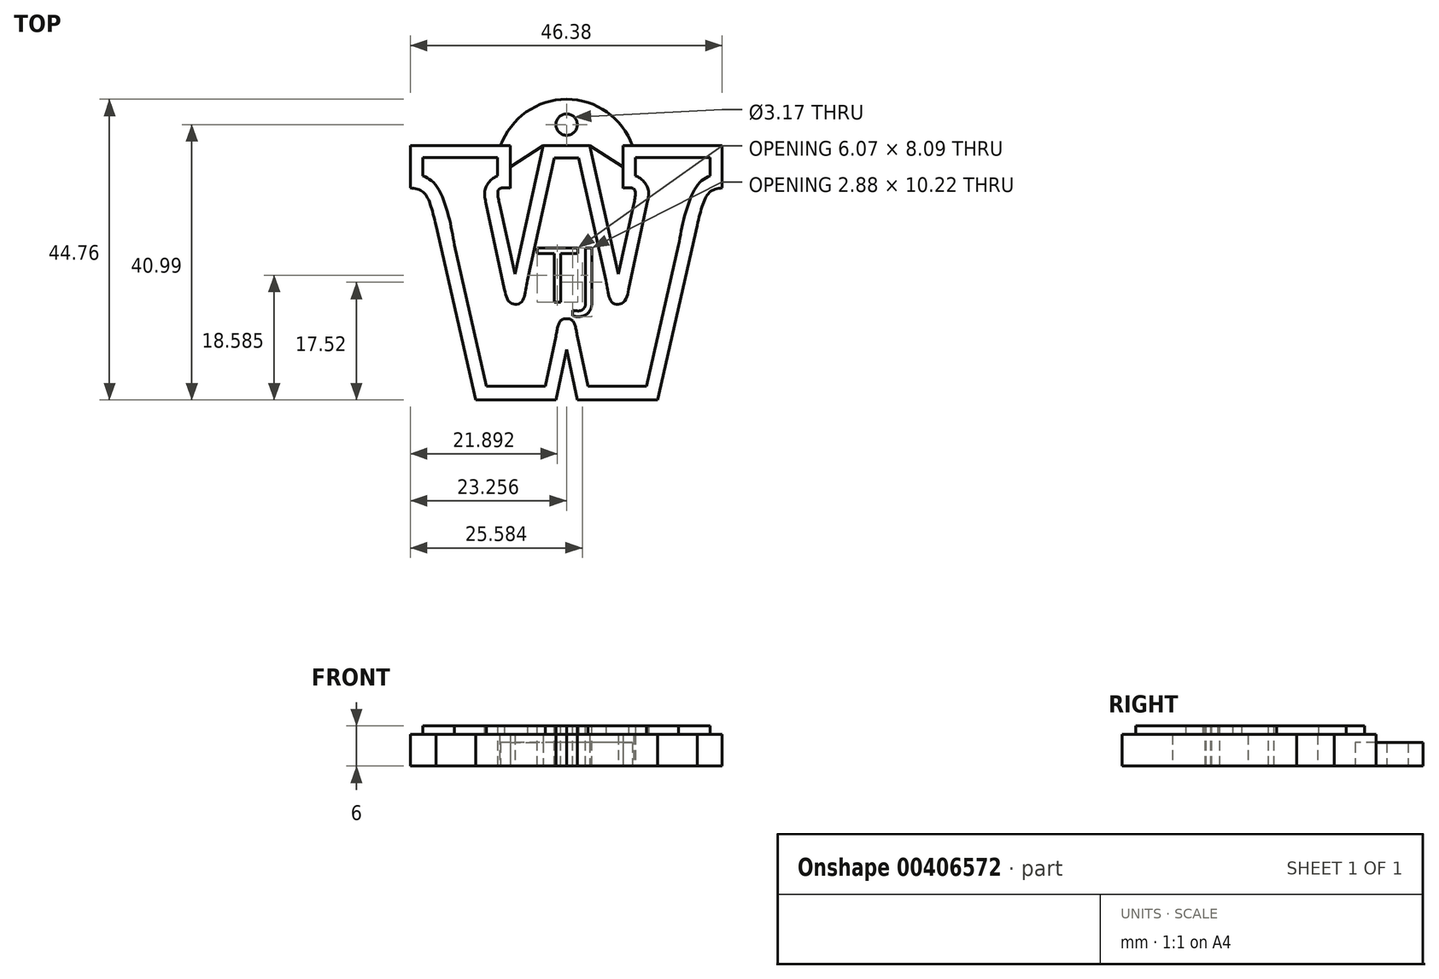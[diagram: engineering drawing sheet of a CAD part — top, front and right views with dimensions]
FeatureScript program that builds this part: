
annotation { "Feature Type Name" : "Feature", "Feature Type Description" : "" }
export const myFeature = defineFeature(function(context is Context, id is Id, definition is map)
    precondition{}
    {
        {
            var Q0;
            Q0=qCreatedBy(makeId("Top.planeOp"),FACE);
            var sketch = newSketch(context, id + "F0", { "sketchPlane" : qUnion([Q0])});
            skLineSegment(sketch, "E0", {"start": v(22.6, 19.1) * mm, "end": v(22.6, 12.57) * mm});
            skLineSegment(sketch, "E1", {"start": v(-0.52, 18.96) * mm, "end": v(-3.98, 18.96) * mm});
            skLineSegment(sketch, "E2", {"start": v(-23.78, 18.96) * mm, "end": v(-23.78, 12.7) * mm});
            skFitSpline(sketch, "E3", {"points": [v(-23.78, 12.7) * mm, v(-22.12, 12.3) * mm, v(-21.04, 10.88) * mm, v(-19.95, 7.12) * mm], "startDerivative": vector(6.33, -0.76) * mm, "endDerivative": vector(2.32, -9.74) * mm});
            skLineSegment(sketch, "E4", {"start": v(-19.95, 7.12) * mm, "end": v(-14.05, -18.87) * mm});
            skLineSegment(sketch, "E5", {"start": v(-14.05, -18.87) * mm, "end": v(-2.12, -18.87) * mm});
            skLineSegment(sketch, "E6", {"start": v(-2.12, -18.87) * mm, "end": v(-0.52, -11.39) * mm});
            skLineSegment(sketch, "E7", {"start": v(-8.89, 18.96) * mm, "end": v(-8.89, 12.65) * mm});
            skFitSpline(sketch, "E8", {"points": [v(-8.89, 12.65) * mm, v(-10.35, 12.65) * mm, v(-10.72, 12.17) * mm, v(-10.5, 10.22) * mm], "startDerivative": vector(-4.74, 0.51) * mm, "endDerivative": vector(1.08, -5.44) * mm});
            skLineSegment(sketch, "E9", {"start": v(-10.5, 10.22) * mm, "end": v(-8.19, -0.13) * mm});
            skLineSegment(sketch, "E10", {"start": v(-8.19, -0.13) * mm, "end": v(-3.98, 18.96) * mm});
            skLineSegment(sketch, "E11", {"start": v(-21.88, 17.2) * mm, "end": v(-10.78, 17.2) * mm});
            skLineSegment(sketch, "E12", {"start": v(-10.78, 17.2) * mm, "end": v(-10.78, 14.5) * mm});
            skLineSegment(sketch, "E13", {"start": v(-21.88, 17.2) * mm, "end": v(-21.88, 14.5) * mm});
            skFitSpline(sketch, "E14", {"points": [v(-21.88, 14.5) * mm, v(-20.1, 13.24) * mm, v(-18.18, 8.9) * mm, v(-17.2, 4.16) * mm], "startDerivative": vector(7.4, -3.57) * mm, "endDerivative": vector(2.13, -12.3) * mm});
            skLineSegment(sketch, "E15", {"start": v(-17.2, 4.16) * mm, "end": v(-12.43, -16.83) * mm});
            skLineSegment(sketch, "E16", {"start": v(-12.43, -16.83) * mm, "end": v(-3.69, -16.83) * mm});
            skLineSegment(sketch, "E17", {"start": v(-3.69, -16.83) * mm, "end": v(-2.1, -9.4) * mm});
            skFitSpline(sketch, "E18", {"points": [v(-2.1, -9.4) * mm, v(-1.63, -7.4) * mm, v(-1.06, -6.82) * mm, v(-0.52, -6.82) * mm], "startDerivative": vector(0.74, 4.85) * mm, "endDerivative": vector(2.26, -0.35) * mm});
            skFitSpline(sketch, "E19", {"points": [v(-10.78, 14.5) * mm, v(-11.85, 13.81) * mm, v(-12.7, 12.25) * mm, v(-12.5, 10.38) * mm], "startDerivative": vector(-3.75, -1.85) * mm, "endDerivative": vector(1.24, -5.26) * mm});
            skLineSegment(sketch, "E20", {"start": v(-12.5, 10.38) * mm, "end": v(-9.75, -2.4) * mm});
            skFitSpline(sketch, "E21", {"points": [v(-9.75, -2.4) * mm, v(-9.14, -4.15) * mm, v(-8.07, -4.65) * mm, v(-7.16, -4.2) * mm, v(-6.7, -2.9) * mm, v(-6.36, -1.1) * mm], "startDerivative": vector(1.75, -8.8) * mm, "endDerivative": vector(1.51, 8.1) * mm});
            skLineSegment(sketch, "E22", {"start": v(-6.36, -1.1) * mm, "end": v(-2.33, 17.18) * mm});
            skLineSegment(sketch, "E23", {"start": v(-2.33, 17.18) * mm, "end": v(-0.52, 17.18) * mm});
            skLineSegment(sketch, "E24.trimOffspring", {"start": v(-8.89, 18.96) * mm, "end": v(-23.78, 18.96) * mm});
            skLineSegment(sketch, "E25.MirrorCS", {"start": v(-0.52, 18.96) * mm, "end": v(2.93, 18.96) * mm});
            skLineSegment(sketch, "E26.MirrorCS", {"start": v(1.28, 17.18) * mm, "end": v(-0.52, 17.18) * mm});
            skLineSegment(sketch, "E27.MirrorCS", {"start": v(5.3, -1.1) * mm, "end": v(1.28, 17.18) * mm});
            skLineSegment(sketch, "E28.MirrorCS", {"start": v(7.14, -0.13) * mm, "end": v(2.93, 18.96) * mm});
            skLineSegment(sketch, "E29.MirrorCS", {"start": v(11.45, 10.38) * mm, "end": v(8.7, -2.4) * mm});
            skFitSpline(sketch, "E30.MirrorCS", {"points": [v(8.7, -2.4) * mm, v(8.1, -4.15) * mm, v(7.03, -4.65) * mm, v(6.11, -4.2) * mm, v(5.65, -2.9) * mm, v(5.3, -1.1) * mm], "startDerivative": vector(-1.75, -8.8) * mm, "endDerivative": vector(-1.51, 8.1) * mm});
            skFitSpline(sketch, "E31.MirrorCS", {"points": [v(9.73, 14.5) * mm, v(10.8, 13.81) * mm, v(11.64, 12.25) * mm, v(11.45, 10.38) * mm], "startDerivative": vector(3.75, -1.85) * mm, "endDerivative": vector(-1.24, -5.26) * mm});
            skFitSpline(sketch, "E32.MirrorCS", {"points": [v(7.84, 12.65) * mm, v(9.3, 12.65) * mm, v(9.67, 12.17) * mm, v(9.46, 10.22) * mm], "startDerivative": vector(4.74, 0.51) * mm, "endDerivative": vector(-1.08, -5.44) * mm});
            skLineSegment(sketch, "E33.MirrorCS", {"start": v(7.84, 18.96) * mm, "end": v(7.84, 12.65) * mm});
            skLineSegment(sketch, "E34.MirrorCS", {"start": v(9.73, 17.2) * mm, "end": v(9.73, 14.5) * mm});
            skLineSegment(sketch, "E35.MirrorCS", {"start": v(7.84, 18.96) * mm, "end": v(22.73, 18.96) * mm});
            skLineSegment(sketch, "E36.MirrorCS", {"start": v(20.83, 17.2) * mm, "end": v(9.73, 17.2) * mm});
            skLineSegment(sketch, "E37.MirrorCS", {"start": v(22.73, 18.96) * mm, "end": v(22.73, 12.7) * mm});
            skLineSegment(sketch, "E38.MirrorCS", {"start": v(20.83, 17.2) * mm, "end": v(20.83, 14.5) * mm});
            skFitSpline(sketch, "E39.MirrorCS", {"points": [v(22.73, 12.7) * mm, v(21.08, 12.3) * mm, v(19.99, 10.88) * mm, v(18.9, 7.12) * mm], "startDerivative": vector(-6.33, -0.76) * mm, "endDerivative": vector(-2.32, -9.74) * mm});
            skLineSegment(sketch, "E40.MirrorCS", {"start": v(18.9, 7.12) * mm, "end": v(13, -18.87) * mm});
            skLineSegment(sketch, "E41.MirrorCS", {"start": v(16.14, 4.16) * mm, "end": v(11.38, -16.83) * mm});
            skFitSpline(sketch, "E42.MirrorCS", {"points": [v(20.83, 14.5) * mm, v(19.04, 13.24) * mm, v(17.13, 8.9) * mm, v(16.14, 4.16) * mm], "startDerivative": vector(-7.4, -3.57) * mm, "endDerivative": vector(-2.13, -12.3) * mm});
            skLineSegment(sketch, "E43.MirrorCS", {"start": v(11.38, -16.83) * mm, "end": v(2.64, -16.83) * mm});
            skLineSegment(sketch, "E44.MirrorCS", {"start": v(13, -18.87) * mm, "end": v(1.07, -18.87) * mm});
            skLineSegment(sketch, "E45.MirrorCS", {"start": v(1.07, -18.87) * mm, "end": v(-0.52, -11.39) * mm});
            skLineSegment(sketch, "E46.MirrorCS", {"start": v(2.64, -16.83) * mm, "end": v(1.06, -9.4) * mm});
            skFitSpline(sketch, "E47.MirrorCS", {"points": [v(1.06, -9.4) * mm, v(0.58, -7.4) * mm, v(0, -6.82) * mm, v(-0.52, -6.82) * mm], "startDerivative": vector(-0.74, 4.85) * mm, "endDerivative": vector(-2.26, -0.35) * mm});
            skLineSegment(sketch, "E48.MirrorCS", {"start": v(9.46, 10.22) * mm, "end": v(7.14, -0.13) * mm});
            skArc(sketch, "E49", {"start": v(9.28, 18.96) * mm, "mid": v(-0.52, 25.89) * mm, "end": v(-10.33, 18.96) * mm});
            skCircle(sketch, "E50", {"center": v(-0.52, 22.12) * mm, "radius": 1.59 * mm});
            skLineSegment(sketch, "E51", {"start": v(-3.98, 18.96) * mm, "end": v(2.93, 18.96) * mm});
            skLineSegment(sketch, "E52", {"start": v(-8.89, 15.8) * mm, "end": v(-3.98, 18.96) * mm});
            skLineSegment(sketch, "E53", {"start": v(7.84, 15.8) * mm, "end": v(2.93, 18.96) * mm});
            skSolve(sketch);
        }
        {
            var Q0;
            Q0=makeQuery(id+"F0.imprint","IMPRINT",FACE,{"disambiguationData":[TD([[makeQuery(id+"F0.imprint","IMPRINT",EDGE,{"derivedFrom":sQuery(id+"F0.wireOp",EDGE,"E11")}),-1.0]])]});
            extrude(context, id + "F1", {"entities" : qUnion([Q0]), "depth" : 6 * mm});
        }
        {
            var Q0;
            {var subQ12=sQuery(id+"F0.wireOp",EDGE,"E2");Q0=makeQuery(id+"F0.imprint","IMPRINT",FACE,{"disambiguationData":[TD([[makeQuery(id+"F0.imprint","IMPRINT",EDGE,{"derivedFrom":subQ12}),1.0]])]});}
            extrude(context, id + "F2", {"entities" : qUnion([Q0]), "operationType" : NewBodyOperationType.ADD, "depth" : 4.7 * mm});
        }
        {
            var Q0;
            {var subQ0=sQuery(id+"F0.wireOp",EDGE,"E49");Q0=makeQuery(id+"F0.imprint","IMPRINT",FACE,{"disambiguationData":[TD([[makeQuery(id+"F0.imprint","IMPRINT",EDGE,{"derivedFrom":subQ0}),1.0]])]});}
            extrude(context, id + "F3", {"entities" : qUnion([Q0]), "operationType" : NewBodyOperationType.ADD, "depth" : 3.5 * mm});
        }
        {
            var Q0;
            Q0=makeQuery(id+"F1.opExtrude","CAP_FACE",FACE,{"disambiguationData":[OSD([sQuery(id+"F0.wireOp",EDGE,"E11"),sQuery(id+"F0.wireOp",EDGE,"E12"),sQuery(id+"F0.wireOp",EDGE,"E13"),sQuery(id+"F0.wireOp",EDGE,"E14"),sQuery(id+"F0.wireOp",EDGE,"E15"),sQuery(id+"F0.wireOp",EDGE,"E16"),sQuery(id+"F0.wireOp",EDGE,"E17"),sQuery(id+"F0.wireOp",EDGE,"E18"),sQuery(id+"F0.wireOp",EDGE,"E19"),sQuery(id+"F0.wireOp",EDGE,"E20"),sQuery(id+"F0.wireOp",EDGE,"E21"),sQuery(id+"F0.wireOp",EDGE,"E22"),sQuery(id+"F0.wireOp",EDGE,"E23"),sQuery(id+"F0.wireOp",EDGE,"E26.MirrorCS"),sQuery(id+"F0.wireOp",EDGE,"E27.MirrorCS"),sQuery(id+"F0.wireOp",EDGE,"E29.MirrorCS"),sQuery(id+"F0.wireOp",EDGE,"E30.MirrorCS"),sQuery(id+"F0.wireOp",EDGE,"E31.MirrorCS"),sQuery(id+"F0.wireOp",EDGE,"E34.MirrorCS"),sQuery(id+"F0.wireOp",EDGE,"E36.MirrorCS"),sQuery(id+"F0.wireOp",EDGE,"E38.MirrorCS"),sQuery(id+"F0.wireOp",EDGE,"E41.MirrorCS"),sQuery(id+"F0.wireOp",EDGE,"E42.MirrorCS"),sQuery(id+"F0.wireOp",EDGE,"E43.MirrorCS"),sQuery(id+"F0.wireOp",EDGE,"E46.MirrorCS"),sQuery(id+"F0.wireOp",EDGE,"E47.MirrorCS")])],"isStart":false});
            var sketch = newSketch(context, id + "F4", { "sketchPlane" : qUnion([Q0])});
            skText(sketch, "E54", { "text": "TJ", "fontName": "OpenSans-Regular.ttf"});
            const initialGuessF4  = {"E54": [-0.00502, -0.00433, 1, 0, 0.00816]};
            skSetInitialGuess(sketch, initialGuessF4);
            skSolve(sketch);
        }
        {
            var Q0;
            Q0=makeQuery(id+"F4.imprint","IMPRINT",FACE,{"disambiguationData":[TD([[makeQuery(id+"F4.imprint","IMPRINT",EDGE,{"derivedFrom":sQuery(id+"F4.wireOp",EDGE,"E54.sketch_text.stroke-0")}),-1.0]])]});
            var Q1;
            Q1=makeQuery(id+"F4.imprint","IMPRINT",FACE,{"disambiguationData":[TD([[makeQuery(id+"F4.imprint","IMPRINT",EDGE,{"derivedFrom":sQuery(id+"F4.wireOp",EDGE,"E54.sketch_text.stroke-8")}),-1.0]])]});
            extrude(context, id + "F5", {"entities" : qUnion([Q0, Q1]), "operationType" : NewBodyOperationType.REMOVE, "oppositeDirection" : true, "depth" : 25 * mm});
        }
    });
